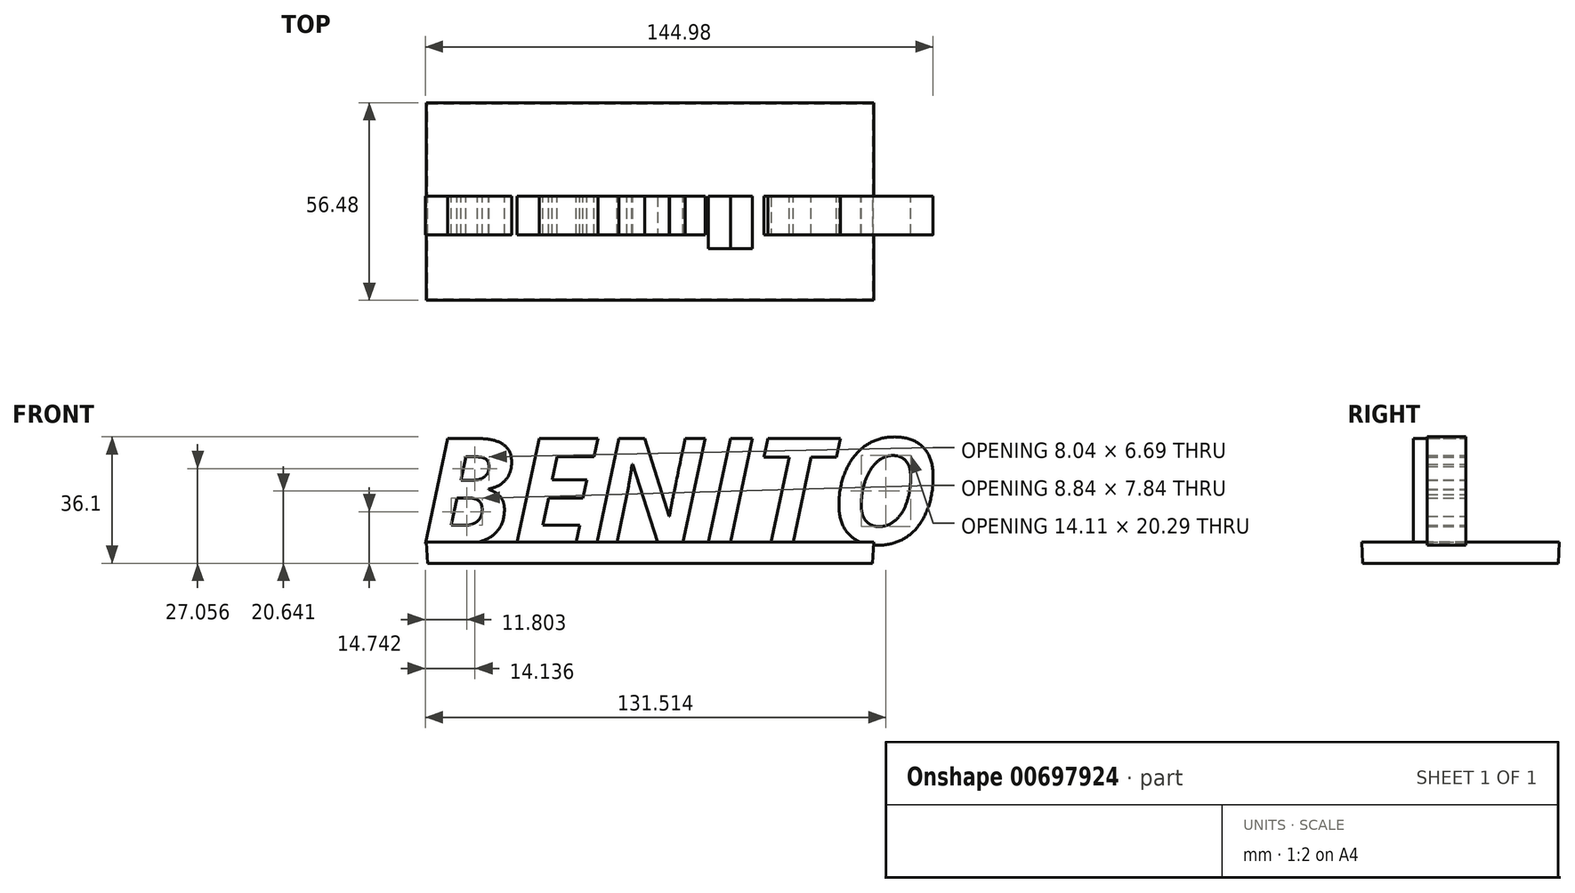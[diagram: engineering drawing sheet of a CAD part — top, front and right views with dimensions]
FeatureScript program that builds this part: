
annotation { "Feature Type Name" : "Feature", "Feature Type Description" : "" }
export const myFeature = defineFeature(function(context is Context, id is Id, definition is map)
    precondition{}
    {
        {
            var Q0;
            Q0=qCreatedBy(makeId("Top.planeOp"),FACE);
            var sketch = newSketch(context, id + "F0", { "sketchPlane" : qUnion([Q0])});
            skLineSegment(sketch, "E0.bottom", {"start": v(-60.91, 26.43) * mm, "end": v(66.16, 26.43) * mm});
            skLineSegment(sketch, "E0.top", {"start": v(-60.91, -29.42) * mm, "end": v(66.16, -29.42) * mm});
            skLineSegment(sketch, "E0.left", {"start": v(-60.91, 26.43) * mm, "end": v(-60.91, -29.42) * mm});
            skLineSegment(sketch, "E0.right", {"start": v(66.16, 26.43) * mm, "end": v(66.16, -29.42) * mm});
            skSolve(sketch);
        }
        {
            var Q0;
            Q0=makeQuery(id+"F0.imprint","IMPRINT",FACE,{"disambiguationData":[TD([[makeQuery(id+"F0.imprint","IMPRINT",EDGE,{"derivedFrom":sQuery(id+"F0.wireOp",EDGE,"E0.bottom")}),-1.0]])]});
            extrude(context, id + "F1", {"entities" : qUnion([Q0]), "depth" : 6 * mm, "offsetDistance" : 25 * mm, "hasDraft" : true, "draftAngle" : 3 * degree});
        }
        {
            var Q0;
            Q0=qCreatedBy(makeId("Front.planeOp"),FACE);
            var sketch = newSketch(context, id + "F2", { "sketchPlane" : qUnion([Q0])});
            skText(sketch, "E1", { "text": "BENITO", "fontName": "OpenSans-BoldItalic.ttf"});
            const initialGuessF2  = {"E1": [-0.0626, 0.00556, 1, 0, 0.03032]};
            skSetInitialGuess(sketch, initialGuessF2);
            skSolve(sketch);
        }
        {
            var Q0;
            Q0=qSketchRegion(id+"F2",true);
            extrude(context, id + "F3", {"entities" : qUnion([Q0]), "operationType" : NewBodyOperationType.ADD, "depth" : 15 * mm, "offsetDistance" : 25 * mm});
        }
        {
            var Q0;
            Q0=makeQuery(id+"F3.opExtrude","CAP_FACE",FACE,{"disambiguationData":[OSD([sQuery(id+"F2.wireOp",EDGE,"E1.sketch_text.stroke-0"),sQuery(id+"F2.wireOp",EDGE,"E1.sketch_text.stroke-1"),sQuery(id+"F2.wireOp",EDGE,"E1.sketch_text.stroke-2"),sQuery(id+"F2.wireOp",EDGE,"E1.sketch_text.stroke-3"),sQuery(id+"F2.wireOp",EDGE,"E1.sketch_text.stroke-4"),sQuery(id+"F2.wireOp",EDGE,"E1.sketch_text.stroke-5"),sQuery(id+"F2.wireOp",EDGE,"E1.sketch_text.stroke-6"),sQuery(id+"F2.wireOp",EDGE,"E1.sketch_text.stroke-7"),sQuery(id+"F2.wireOp",EDGE,"E1.sketch_text.stroke-8"),sQuery(id+"F2.wireOp",EDGE,"E1.sketch_text.stroke-9"),sQuery(id+"F2.wireOp",EDGE,"E1.sketch_text.stroke-10"),sQuery(id+"F2.wireOp",EDGE,"E1.sketch_text.stroke-11"),sQuery(id+"F2.wireOp",EDGE,"E1.sketch_text.stroke-12"),sQuery(id+"F2.wireOp",EDGE,"E1.sketch_text.stroke-13"),sQuery(id+"F2.wireOp",EDGE,"E1.sketch_text.stroke-14")])],"isStart":false});
            var Q1;
            Q1=makeQuery(id+"F3.opExtrude","CAP_FACE",FACE,{"disambiguationData":[OSD([sQuery(id+"F2.wireOp",EDGE,"E1.sketch_text.stroke-15"),sQuery(id+"F2.wireOp",EDGE,"E1.sketch_text.stroke-16"),sQuery(id+"F2.wireOp",EDGE,"E1.sketch_text.stroke-17"),sQuery(id+"F2.wireOp",EDGE,"E1.sketch_text.stroke-18"),sQuery(id+"F2.wireOp",EDGE,"E1.sketch_text.stroke-19"),sQuery(id+"F2.wireOp",EDGE,"E1.sketch_text.stroke-20"),sQuery(id+"F2.wireOp",EDGE,"E1.sketch_text.stroke-21"),sQuery(id+"F2.wireOp",EDGE,"E1.sketch_text.stroke-22"),sQuery(id+"F2.wireOp",EDGE,"E1.sketch_text.stroke-23"),sQuery(id+"F2.wireOp",EDGE,"E1.sketch_text.stroke-24"),sQuery(id+"F2.wireOp",EDGE,"E1.sketch_text.stroke-25"),sQuery(id+"F2.wireOp",EDGE,"E1.sketch_text.stroke-26"),sQuery(id+"F2.wireOp",EDGE,"E1.sketch_text.stroke-27"),sQuery(id+"F2.wireOp",EDGE,"E1.sketch_text.stroke-28"),sQuery(id+"F2.wireOp",EDGE,"E1.sketch_text.stroke-29"),sQuery(id+"F2.wireOp",EDGE,"E1.sketch_text.stroke-30"),sQuery(id+"F2.wireOp",EDGE,"E1.sketch_text.stroke-31"),sQuery(id+"F2.wireOp",EDGE,"E1.sketch_text.stroke-32"),sQuery(id+"F2.wireOp",EDGE,"E1.sketch_text.stroke-33"),sQuery(id+"F2.wireOp",EDGE,"E1.sketch_text.stroke-34"),sQuery(id+"F2.wireOp",EDGE,"E1.sketch_text.stroke-35"),sQuery(id+"F2.wireOp",EDGE,"E1.sketch_text.stroke-36"),sQuery(id+"F2.wireOp",EDGE,"E1.sketch_text.stroke-37"),sQuery(id+"F2.wireOp",EDGE,"E1.sketch_text.stroke-38"),sQuery(id+"F2.wireOp",EDGE,"E1.sketch_text.stroke-39")])],"isStart":false});
            var Q2;
            Q2=makeQuery(id+"F3.opExtrude","CAP_FACE",FACE,{"disambiguationData":[OSD([sQuery(id+"F2.wireOp",EDGE,"E1.sketch_text.stroke-40"),sQuery(id+"F2.wireOp",EDGE,"E1.sketch_text.stroke-41"),sQuery(id+"F2.wireOp",EDGE,"E1.sketch_text.stroke-42"),sQuery(id+"F2.wireOp",EDGE,"E1.sketch_text.stroke-43"),sQuery(id+"F2.wireOp",EDGE,"E1.sketch_text.stroke-44"),sQuery(id+"F2.wireOp",EDGE,"E1.sketch_text.stroke-45"),sQuery(id+"F2.wireOp",EDGE,"E1.sketch_text.stroke-46"),sQuery(id+"F2.wireOp",EDGE,"E1.sketch_text.stroke-47"),sQuery(id+"F2.wireOp",EDGE,"E1.sketch_text.stroke-48"),sQuery(id+"F2.wireOp",EDGE,"E1.sketch_text.stroke-49"),sQuery(id+"F2.wireOp",EDGE,"E1.sketch_text.stroke-50"),sQuery(id+"F2.wireOp",EDGE,"E1.sketch_text.stroke-51"),sQuery(id+"F2.wireOp",EDGE,"E1.sketch_text.stroke-52"),sQuery(id+"F2.wireOp",EDGE,"E1.sketch_text.stroke-53"),sQuery(id+"F2.wireOp",EDGE,"E1.sketch_text.stroke-54"),sQuery(id+"F2.wireOp",EDGE,"E1.sketch_text.stroke-55"),sQuery(id+"F2.wireOp",EDGE,"E1.sketch_text.stroke-56"),sQuery(id+"F2.wireOp",EDGE,"E1.sketch_text.stroke-57")])],"isStart":false});
            var Q3;
            Q3=makeQuery(id+"F3.opExtrude","CAP_FACE",FACE,{"disambiguationData":[OSD([sQuery(id+"F2.wireOp",EDGE,"E1.sketch_text.stroke-58"),sQuery(id+"F2.wireOp",EDGE,"E1.sketch_text.stroke-59"),sQuery(id+"F2.wireOp",EDGE,"E1.sketch_text.stroke-60"),sQuery(id+"F2.wireOp",EDGE,"E1.sketch_text.stroke-61")])],"isStart":false});
            var Q4;
            Q4=makeQuery(id+"F3.opExtrude","CAP_FACE",FACE,{"disambiguationData":[OSD([sQuery(id+"F2.wireOp",EDGE,"E1.sketch_text.stroke-62"),sQuery(id+"F2.wireOp",EDGE,"E1.sketch_text.stroke-63"),sQuery(id+"F2.wireOp",EDGE,"E1.sketch_text.stroke-64"),sQuery(id+"F2.wireOp",EDGE,"E1.sketch_text.stroke-65"),sQuery(id+"F2.wireOp",EDGE,"E1.sketch_text.stroke-66"),sQuery(id+"F2.wireOp",EDGE,"E1.sketch_text.stroke-67"),sQuery(id+"F2.wireOp",EDGE,"E1.sketch_text.stroke-68"),sQuery(id+"F2.wireOp",EDGE,"E1.sketch_text.stroke-69"),sQuery(id+"F2.wireOp",EDGE,"E1.sketch_text.stroke-70"),sQuery(id+"F2.wireOp",EDGE,"E1.sketch_text.stroke-71"),sQuery(id+"F2.wireOp",EDGE,"E1.sketch_text.stroke-72"),sQuery(id+"F2.wireOp",EDGE,"E1.sketch_text.stroke-73"),sQuery(id+"F2.wireOp",EDGE,"E1.sketch_text.stroke-74"),sQuery(id+"F2.wireOp",EDGE,"E1.sketch_text.stroke-75"),sQuery(id+"F2.wireOp",EDGE,"E1.sketch_text.stroke-76"),sQuery(id+"F2.wireOp",EDGE,"E1.sketch_text.stroke-77"),sQuery(id+"F2.wireOp",EDGE,"E1.sketch_text.stroke-78"),sQuery(id+"F2.wireOp",EDGE,"E1.sketch_text.stroke-79"),sQuery(id+"F2.wireOp",EDGE,"E1.sketch_text.stroke-80"),sQuery(id+"F2.wireOp",EDGE,"E1.sketch_text.stroke-81"),sQuery(id+"F2.wireOp",EDGE,"E1.sketch_text.stroke-82"),sQuery(id+"F2.wireOp",EDGE,"E1.sketch_text.stroke-83"),sQuery(id+"F2.wireOp",EDGE,"E1.sketch_text.stroke-84"),sQuery(id+"F2.wireOp",EDGE,"E1.sketch_text.stroke-85"),sQuery(id+"F2.wireOp",EDGE,"E1.sketch_text.stroke-86")])],"isStart":false});
            extrude(context, id + "F4", {"entities" : qUnion([Q0, Q1, Q2, Q3, Q4]), "operationType" : NewBodyOperationType.REMOVE, "oppositeDirection" : true, "depth" : 4 * mm, "offsetDistance" : 25 * mm});
        }
    });
